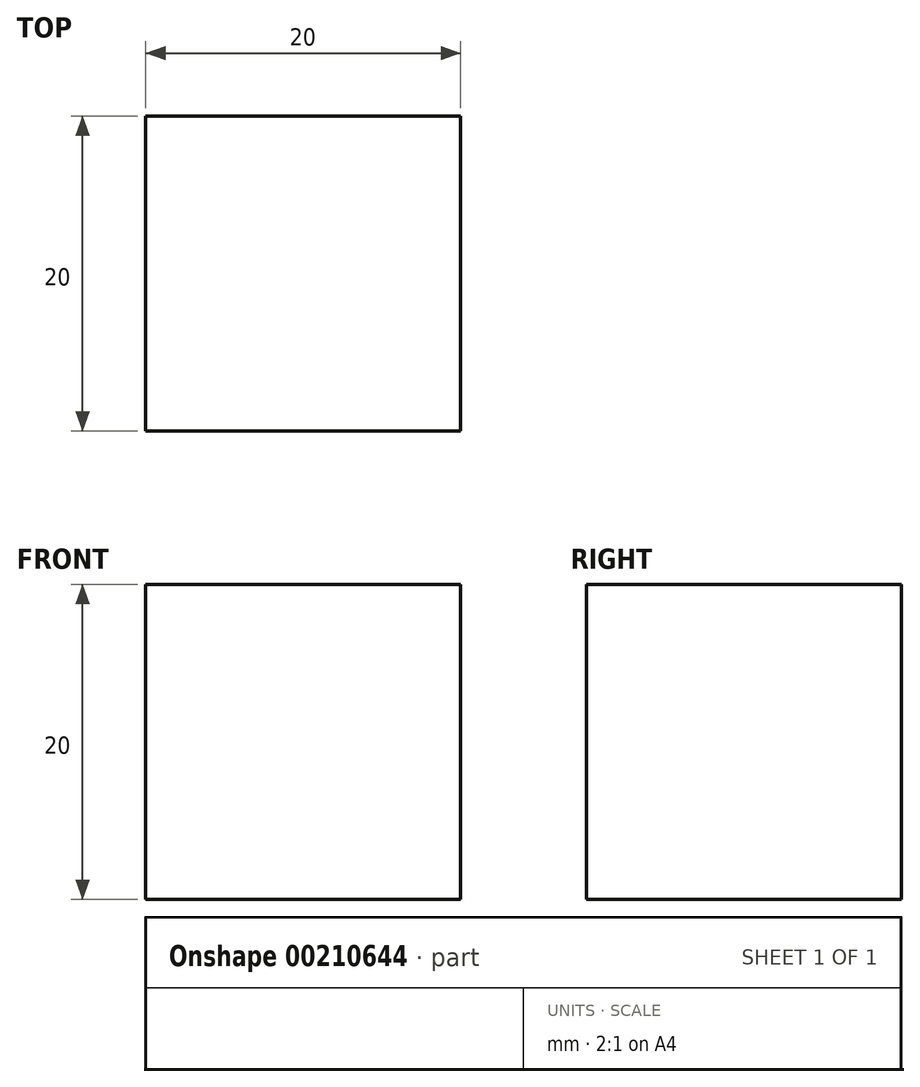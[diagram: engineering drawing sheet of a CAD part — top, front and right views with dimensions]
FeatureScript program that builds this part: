
annotation { "Feature Type Name" : "Feature", "Feature Type Description" : "" }
export const myFeature = defineFeature(function(context is Context, id is Id, definition is map)
    precondition{}
    {
        {
            var Q0;
            Q0=qCreatedBy(makeId("Top.planeOp"),FACE);
            var sketch = newSketch(context, id + "F0", { "sketchPlane" : qUnion([Q0])});
            skLineSegment(sketch, "E0.bottom", {"start": v(0, 0) * mm, "end": v(20, 0) * mm});
            skLineSegment(sketch, "E0.top", {"start": v(0, 20) * mm, "end": v(20, 20) * mm});
            skLineSegment(sketch, "E0.left", {"start": v(0, 0) * mm, "end": v(0, 20) * mm});
            skLineSegment(sketch, "E0.right", {"start": v(20, 0) * mm, "end": v(20, 20) * mm});
            skSolve(sketch);
        }
        {
            var Q0;
            Q0 = qSketchRegion(id + "F0", true);
            extrude(context, id + "F1", {"entities" : qUnion([Q0]), "depth" : 20 * mm});
        }
    });
